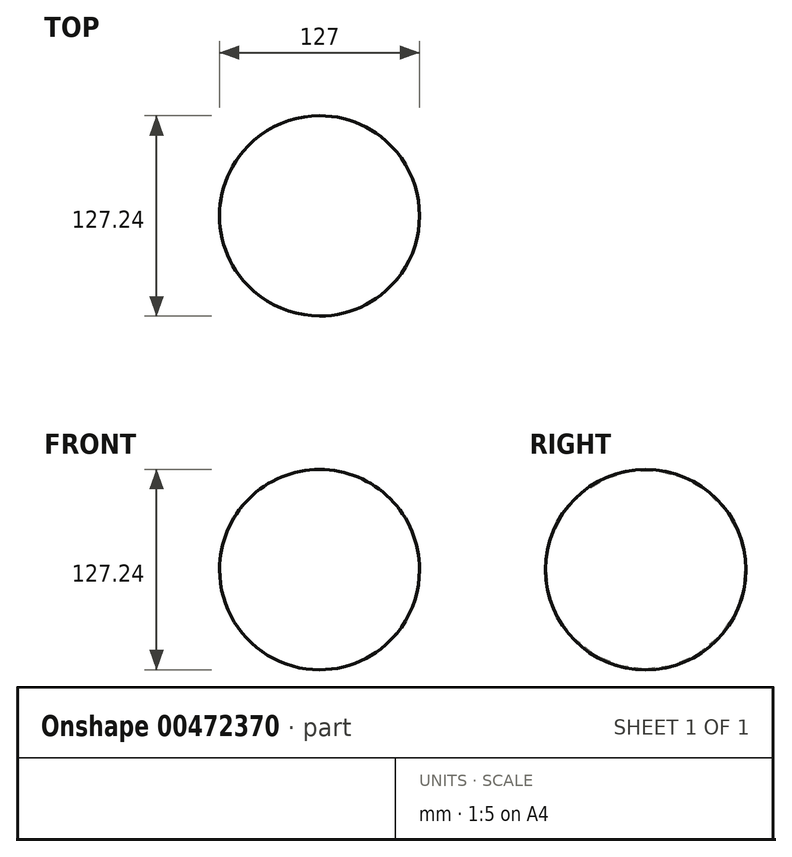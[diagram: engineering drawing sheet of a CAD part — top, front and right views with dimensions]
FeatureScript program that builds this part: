
annotation { "Feature Type Name" : "Feature", "Feature Type Description" : "" }
export const myFeature = defineFeature(function(context is Context, id is Id, definition is map)
    precondition{}
    {
        {
            var Q0;
            Q0=qCreatedBy(makeId("Top.planeOp"),FACE);
            var sketch = newSketch(context, id + "F0", { "sketchPlane" : qUnion([Q0])});
            skLineSegment(sketch, "E0", {"start": v(0, 0) * mm, "end": v(127, 0) * mm});
            skArc(sketch, "E1", {"start": v(127, 0) * mm, "mid": v(63.5, 63.62) * mm, "end": v(0, 0) * mm});
            skSolve(sketch);
        }
        {
            var Q0;
            Q0=makeQuery(id+"F0.imprint","IMPRINT",FACE,{"disambiguationData":[TD([[makeQuery(id+"F0.imprint","IMPRINT",EDGE,{"derivedFrom":sQuery(id+"F0.wireOp",EDGE,"E0")}),1.0]])]});
            var Q1;
            Q1=sQuery(id+"F0.wireOp",EDGE,"E0");
            revolve(context, id + "F1", {"entities" : qUnion([Q0]), "axis" : qUnion([Q1]), "revolveType" : RevolveType.FULL});
        }
    });
